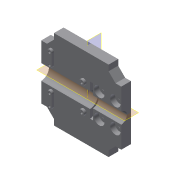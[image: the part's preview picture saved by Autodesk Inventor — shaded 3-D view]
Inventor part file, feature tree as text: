
AUTODESK INVENTOR PART (.ipt)
format: ipt  version: 2022 (Build 260153000, 153)  size: 330,240 bytes
history: native  units: mm
features: reference x20, other x12, sketch x11, extrude x10, plane x6, projected_geometry x5, hole x1
ambient origin geometry x8: Origin, YZ Plane, XZ Plane, XY Plane, X Axis, Y Axis, Z Axis, Center Point
bodies: Solid1 (feature_tree)
feature tree (65):
  plane  "Work Plane1"
  extrude  "Extrusion1"  Depth=53.8mm
  extrude  "IM_offset"  Depth=53.8mm
  plane  "Arbeitsebene5"
  plane  "Arbeitsebene6"
  sketch  "Skizze25"  dims[d21=45.0mm d22=45.0mm]
  plane  "Arbeitsebene7"
  extrude  "Extrusion21"  Depth=45.0mm
  extrude  "Extrusion22"  Depth=20.0mm
  extrude  "Extrusion23"  Depth=2.8mm
  hole  "Bohrung1"  [1 undecoded]
  sketch  "Skizze29"  dims[d36=0.1mm d37=0.1mm]
  plane  "Arbeitsebene8"
  extrude  "Extrusion24"  Depth=0.1mm
  extrude  "Extrusion25"  Depth=0.1mm
  sketch  "Skizze31"  dims[d40=0.2mm d41=10.0mm d42=0.0mm]
  plane  "Arbeitsebene9"
  extrude  "Extrusion26"  Depth=10.0mm TaperAngle=0.0deg
  extrude  "Extrusion27"  Depth=10.0mm
  extrude  "Extrusion28"  Depth=10.0mm
  sketch  "Sketch1"  dims[d10=6.0mm d11=0.0mm d18=53.8mm]
  reference  "Reference1"
  reference  "Reference2"
  reference  "Reference3"
  reference  "Reference4"
  reference  "Reference9"
  reference  "Reference20"
  reference  "Reference21"
  reference  "Reference22"
  reference  "Reference23"
  reference  "Reference24"
  sketch  "Skizze4"  dims[d19=45.0deg d20=53.8mm]
  projected_geometry  "Projizierte Kontur1"
  reference  "Referenz27"
  sketch  "Skizze26"  dims[d30=20.0mm d31=20.0mm]
  reference  "Referenz28"
  sketch  "Skizze27"  dims[d32=2.8mm d33=2.8mm]
  reference  "Referenz29"
  sketch  "Skizze28"  dims[d34=2.8mm d35=3.0mm]
  projected_geometry  "Projizierte Kontur15"
  reference  "Referenz30"
  reference  "Referenz31"
  reference  "Referenz32"
  sketch  "Skizze30"  dims[d38=0.1mm d39=0.1mm]
  projected_geometry  "Projizierte Kontur16"
  reference  "Referenz33"
  projected_geometry  "Projizierte Kontur17"
  sketch  "Skizze32"  dims[d151=10.0mm d152=0.0mm d153=0.5mm]
  reference  "Referenz34"
  reference  "Referenz35"
  sketch  "Skizze33"  dims[d154=1.8mm d155=0.0mm d156=0.5mm d157=0.0mm d158=0.0mm d160=0.3mm d165=10.0mm d166=15.0mm d167=2.8mm d168=6.0mm d169=6.5mm d170=3.0mm d171=90.0deg d172=30.0mm d173=20.594885mm d174=3.5mm d175=3.0mm d176=3.0mm d177=6.0mm d178=0.0mm d179=10.0mm d180=0.0mm d181=3.5mm d182=3.0mm d183=3.0mm d184=10.0mm d185=0.0mm d186=10.0mm d187=0.0mm d188=2.0mm d189=10.0mm d190=0.0mm d161=0.872665mm d162=0.5mm d163=0.872665mm]
  reference  "Referenz36"
  projected_geometry  "Projizierte Kontur18"
  other  "Assembly_Cube_v2_Thorlabs.iam"
  other  "10_Cube_Base:1"
  other  "00_Base_v0:1"
  other  "Assembly_Cube_Kinematic_Mirrormount_v2.iam"
  other  "Assembly_Cube_empty_1x1_v2:1"
  other  "10_Cube_1x1_v2:1"
  other  "10_Lid_1x1_v2:1"
  other  "Assembly_Cube_Syringepump_Micro_v3.iam"
  other  "00_Syringe_10ml:1"
  other  "00_Microlinearmotor_aliexpress_5mm:1"
  other  "00_Microlinearmotor_aliexpress_5mm:2"
  other  "10_Cube_Lid:1"
note: 1 required parameter value undecoded (feature->parameter linkage not recoverable at this tier; creation-order binding heuristic only, values carry confidence <= 0.55)
